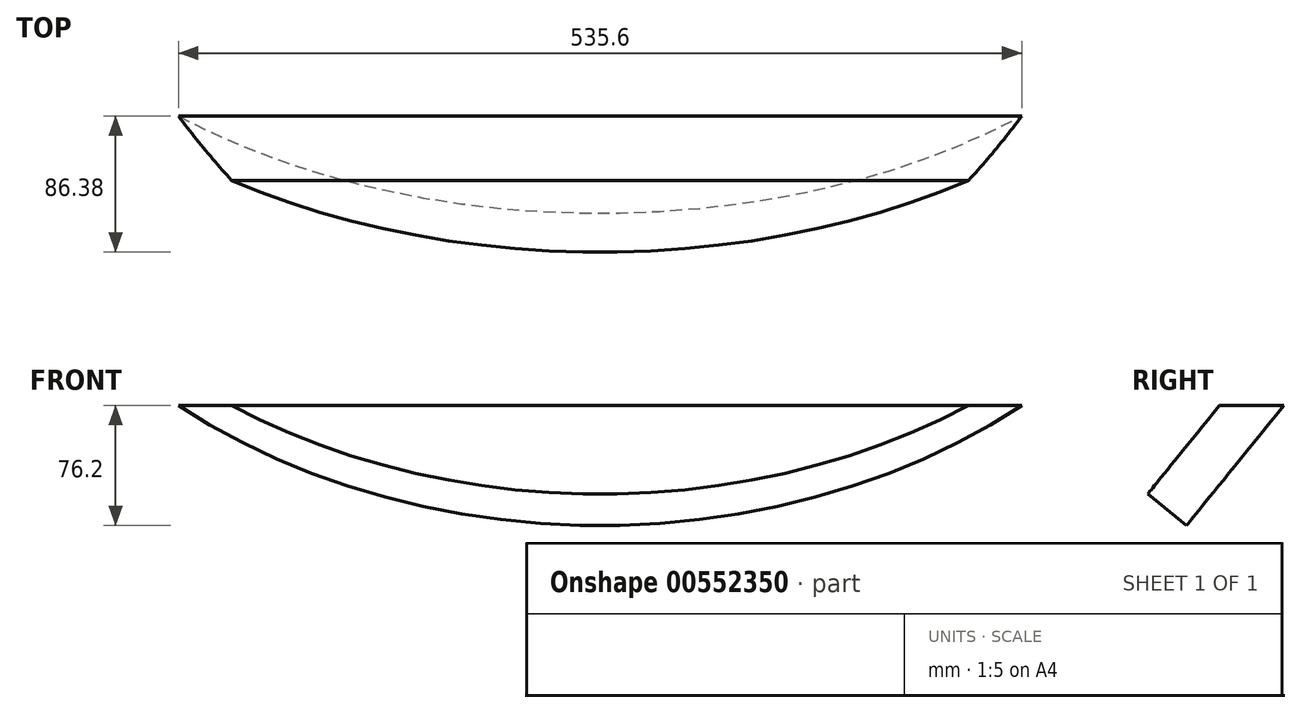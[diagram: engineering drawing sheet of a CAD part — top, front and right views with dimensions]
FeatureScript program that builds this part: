
annotation { "Feature Type Name" : "Feature", "Feature Type Description" : "" }
export const myFeature = defineFeature(function(context is Context, id is Id, definition is map)
    precondition{}
    {
        {
            var Q0;
            Q0=qCreatedBy(makeId("Right.planeOp"),FACE);
            var sketch = newSketch(context, id + "F0", { "sketchPlane" : qUnion([Q0])});
            skLineSegment(sketch, "E0", {"start": v(260.4, -102.8) * mm, "end": v(-200.35, 270.32) * mm});
            skLineSegment(sketch, "E1", {"start": v(260.4, -102.8) * mm, "end": v(-349.2, -102.8) * mm});
            skLineSegment(sketch, "E2", {"start": v(27.4, -102.8) * mm, "end": v(27.4, 85.89) * mm});
            skLineSegment(sketch, "E3", {"start": v(-43.52, 143.32) * mm, "end": v(-304.52, -179) * mm});
            skSolve(sketch);
        }
        {
            var Q0;
            {var subQ0=sQuery(id+"F0.wireOp",EDGE,"E2");Q0=makeQuery(id+"F0.imprint","IMPRINT",FACE,{"disambiguationData":[TD([[makeQuery(id+"F0.imprint","IMPRINT",EDGE,{"derivedFrom":subQ0}),1.0]])]});}
            extrude(context, id + "F1", {"entities" : qUnion([Q0]), "depth" : 25.4 * mm, "offsetDistance" : 25.4 * mm});
        }
        {
            var Q0;
            Q0=makeQuery(id+"F1.opExtrude","SWEPT_FACE",FACE,{"disambiguationData":[OSD([sQuery(id+"F0.wireOp",EDGE,"E3")])]});
            var sketch = newSketch(context, id + "F2", { "sketchPlane" : qUnion([Q0])});
            skCircle(sketch, "E4", {"center": v(12.7, 83.99) * mm, "radius": 414.73 * mm});
            skLineSegment(sketch, "E5", {"start": v(12.7, -232.7) * mm, "end": v(-255.1, -232.7) * mm});
            skLineSegment(sketch, "E6", {"start": v(-255.1, -232.7) * mm, "end": v(280.5, -232.7) * mm});
            skSolve(sketch);
        }
        {
            var Q0;
            Q0=makeQuery(id+"F2.imprint","IMPRINT",FACE,{"disambiguationData":[TD([[makeQuery(id+"F2.imprint","IMPRINT",EDGE,{"derivedFrom":sQuery(id+"F2.wireOp",EDGE,"E4")}),1.0]])]});
            extrude(context, id + "F3", {"entities" : qUnion([Q0]), "depth" : 31.75 * mm, "offsetDistance" : 25.4 * mm});
        }
        {
            var Q0;
            Q0=makeQuery(id+"F1.opExtrude","SWEPT_FACE",FACE,{"disambiguationData":[OSD([sQuery(id+"F0.wireOp",EDGE,"E1")])]});
            var sketch = newSketch(context, id + "F4", { "sketchPlane" : qUnion([Q0])});
            skLineSegment(sketch, "E7", {"start": v(12.7, 242.81) * mm, "end": v(293.9, 242.81) * mm});
            skLineSegment(sketch, "E8", {"start": v(293.9, 242.81) * mm, "end": v(293.9, 285.48) * mm});
            skLineSegment(sketch, "E9", {"start": v(293.9, 285.48) * mm, "end": v(-263.44, 285.48) * mm});
            skLineSegment(sketch, "E10", {"start": v(-263.44, 285.48) * mm, "end": v(-263.44, 242.81) * mm});
            skLineSegment(sketch, "E11", {"start": v(-263.44, 242.81) * mm, "end": v(12.7, 242.81) * mm});
            skSolve(sketch);
        }
        {
            var Q0;
            {var subQ0=sQuery(id+"F4.wireOp",EDGE,"E8");Q0=makeQuery(id+"F4.imprint","IMPRINT",FACE,{"disambiguationData":[TD([[makeQuery(id+"F4.imprint","IMPRINT",EDGE,{"derivedFrom":subQ0}),1.0]])]});}
            extrude(context, id + "F5", {"entities" : qUnion([Q0]), "operationType" : NewBodyOperationType.REMOVE, "oppositeDirection" : true, "depth" : 25.4 * mm, "offsetDistance" : 25.4 * mm});
        }
        {
            var Q0;
            Q0=makeQuery(id+"F1.opExtrude","SWEPT_FACE",FACE,{"disambiguationData":[OSD([sQuery(id+"F0.wireOp",EDGE,"E1")])]});
            var sketch = newSketch(context, id + "F6", { "sketchPlane" : qUnion([Q0])});
            skSolve(sketch);
        }
        {
            var Q0;
            {var subQ0=sQuery(id+"F0.wireOp",EDGE,"E1");Q0=makeQuery(id+"F6.imprint","IMPRINT",FACE,{"disambiguationData":[TD([[makeQuery(id+"F6.imprint","IMPRINT",EDGE,{"derivedFrom":makeQuery(id+"F1.opExtrude","CAP_EDGE",EDGE,{"disambiguationData":[OSD([subQ0])],"isStart":true})}),-1.0]])]});}
            extrude(context, id + "F7", {"entities" : qUnion([Q0]), "operationType" : NewBodyOperationType.REMOVE, "oppositeDirection" : true, "depth" : 508 * mm, "offsetDistance" : 25.4 * mm});
        }
    });
